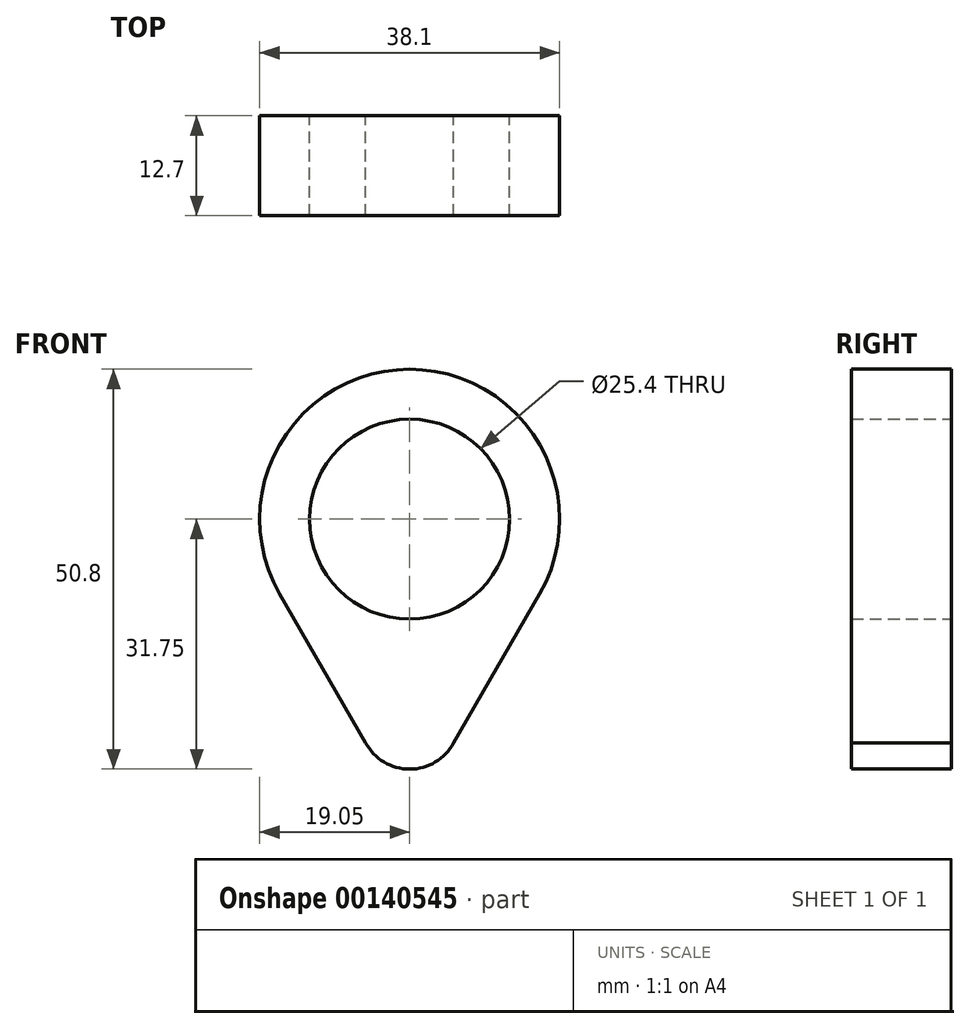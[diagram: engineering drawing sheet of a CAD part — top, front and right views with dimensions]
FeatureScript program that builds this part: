
annotation { "Feature Type Name" : "Feature", "Feature Type Description" : "" }
export const myFeature = defineFeature(function(context is Context, id is Id, definition is map)
    precondition{}
    {
        {
            var Q0;
            Q0=qCreatedBy(makeId("Front.planeOp"),FACE);
            var sketch = newSketch(context, id + "F0", { "sketchPlane" : qUnion([Q0])});
            skCircle(sketch, "E0", {"center": v(0, 0) * mm, "radius": 12.7 * mm});
            skArc(sketch, "E1", {"start": v(16.5, -9.53) * mm, "mid": v(0, 19.05) * mm, "end": v(-16.5, -9.53) * mm});
            skArc(sketch, "E2", {"start": v(-5.59, -28.42) * mm, "mid": v(0, -31.75) * mm, "end": v(5.59, -28.42) * mm});
            skLineSegment(sketch, "E3", {"start": v(5.59, -28.42) * mm, "end": v(16.5, -9.53) * mm});
            skLineSegment(sketch, "E4", {"start": v(-5.59, -28.42) * mm, "end": v(-16.5, -9.53) * mm});
            skSolve(sketch);
        }
        {
            var Q0;
            Q0=makeQuery(id+"F0.imprint","IMPRINT",FACE,{"disambiguationData":[TD([[makeQuery(id+"F0.imprint","IMPRINT",EDGE,{"derivedFrom":sQuery(id+"F0.wireOp",EDGE,"E0")}),-1.0]])]});
            extrude(context, id + "F1", {"entities" : qUnion([Q0]), "endBound" : BoundingType.SYMMETRIC, "depth" : 12.7 * mm});
        }
    });
